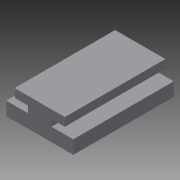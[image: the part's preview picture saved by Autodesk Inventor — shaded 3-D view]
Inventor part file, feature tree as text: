
AUTODESK INVENTOR PART (.ipt)
format: ipt  version: 2014 (Build 180170000, 170)  size: 80,896 bytes
history: native  units: in
note: dims shown in document units (in); Inventor stores cm internally (conversion verified against a paired STEP export)
features: extrude x1, sketch x1
ambient origin geometry x8: Origin, YZ Plane, XZ Plane, XY Plane, X Axis, Y Axis, Z Axis, Center Point
bodies: Solid1 (feature_tree)
feature tree (2):
  extrude  "Extrusion1"  [1 undecoded]
  sketch  "Sketch1"  dims[d0=1.5in d1=0.0in]
note: 1 required parameter value undecoded (feature->parameter linkage not recoverable at this tier; creation-order binding heuristic only, values carry confidence <= 0.55)
